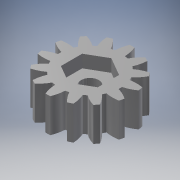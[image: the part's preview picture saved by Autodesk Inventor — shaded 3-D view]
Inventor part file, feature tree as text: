
AUTODESK INVENTOR PART (.ipt)
format: ipt  version: 2017 (Build 210142000, 142)  size: 215,552 bytes
history: native  units: mm (DEFAULTED — no unit token found)
features: sketch x4, extrude x3, plane x3, other x3
ambient origin geometry x8: Origin, YZ Plane, XZ Plane, XY Plane, X Axis, Y Axis, Z Axis, Center Point
bodies: Solid1 (feature_tree)
feature tree (13):
  extrude  "Extrusion1"  Depth=8.0mm TaperAngle=0.0deg
  plane  "Work Plane2"
  plane  "Work Plane8"
  plane  "Work Plane9"
  other  "Spur Gear"
  extrude  "Extrusion2"  Depth=10.0mm TaperAngle=0.0deg
  extrude  "Extrusion3"  Depth=2.243995mm TaperAngle=0.0deg
  sketch  "Sketch1"  dims[d0=20.0mm d1=8.0mm d2=0.0mm]
  sketch  "Sketch2"  dims[d3=17.5mm d4=10.0mm d5=0.0mm]
  other  "Srf1"
  sketch  "Sketch3"  dims[d16=21.25mm d17=0.0mm d34=2.243995mm]
  sketch  "Sketch4"  dims[d39=0.0mm d41=0.0mm d43=21.25mm d46=21.25mm d47=0.0mm d48=0.0mm d49=4.1656mm d50=10.0mm d51=0.0mm d52=10.0838mm d53=3.0mm d54=0.0mm]
  other  "Pitch Diameter"
